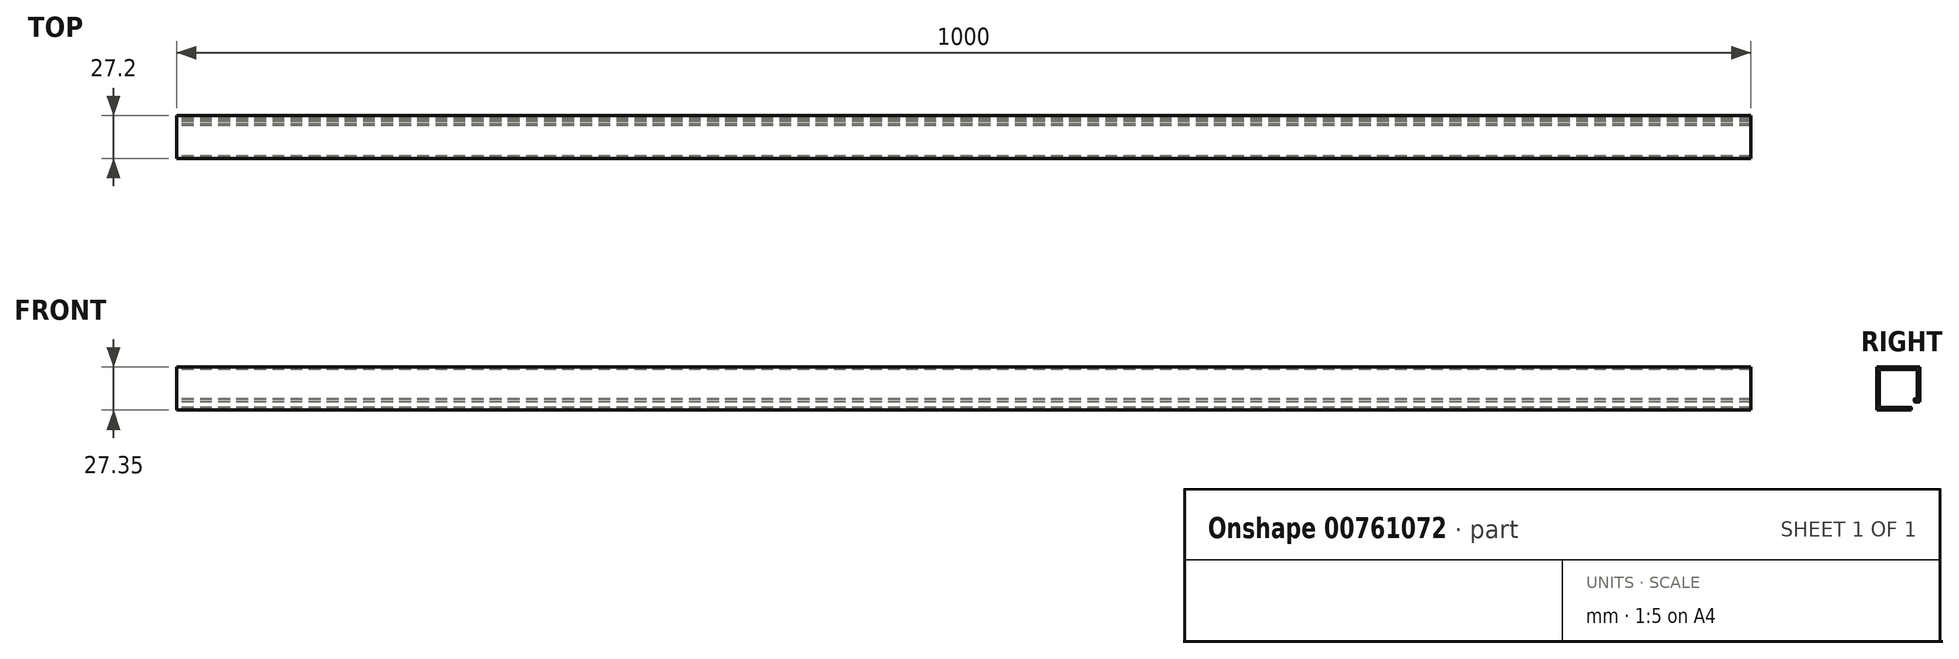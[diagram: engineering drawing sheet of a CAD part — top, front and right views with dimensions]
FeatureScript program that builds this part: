
annotation { "Feature Type Name" : "Feature", "Feature Type Description" : "" }
export const myFeature = defineFeature(function(context is Context, id is Id, definition is map)
    precondition{}
    {
        {
            var Q0;
            Q0=qCreatedBy(makeId("Right.planeOp"),FACE);
            var sketch = newSketch(context, id + "F0", { "sketchPlane" : qUnion([Q0])});
            skLineSegment(sketch, "E0.bottom", {"start": v(27.2, 27.35) * mm, "end": v(0, 27.35) * mm});
            skLineSegment(sketch, "E0.top", {"start": v(22, 0) * mm, "end": v(0, 0) * mm});
            skPoint(sketch, "E0.middle", {"position": v(0, 0) * mm});
            skLineSegment(sketch, "E1", {"start": v(22, 0) * mm, "end": v(22, 1.6) * mm});
            skLineSegment(sketch, "E2", {"start": v(1.6, 25.75) * mm, "end": v(25.6, 25.75) * mm});
            skLineSegment(sketch, "E3", {"start": v(27.2, 5.35) * mm, "end": v(27.2, 27.35) * mm});
            skPoint(sketch, "E4.orphan", {"position": v(13.3, 0) * mm});
            skLineSegment(sketch, "E5", {"start": v(22, 1.6) * mm, "end": v(22, 1.6) * mm});
            skLineSegment(sketch, "E6", {"start": v(21.75, 1.85) * mm, "end": v(21.37, 1.85) * mm});
            skPoint(sketch, "E7.start.orphan", {"position": v(12.8, 0) * mm});
            skLineSegment(sketch, "E8.trimOffspring", {"start": v(21, 1.6) * mm, "end": v(1.6, 1.6) * mm});
            skLineSegment(sketch, "E9.trimOffspring", {"start": v(25.6, 6.95) * mm, "end": v(25.6, 25.75) * mm});
            skLineSegment(sketch, "E10", {"start": v(27.2, 5.35) * mm, "end": v(24.1, 5.35) * mm});
            skLineSegment(sketch, "E11", {"start": v(23.6, 5.85) * mm, "end": v(23.6, 6.95) * mm});
            skLineSegment(sketch, "E12", {"start": v(23.85, 7.2) * mm, "end": v(24.33, 7.2) * mm});
            skLineSegment(sketch, "E13", {"start": v(24.7, 6.95) * mm, "end": v(25.6, 6.95) * mm});
            skPoint(sketch, "E14.visualSharp", {"position": v(23.6, 0) * mm});
            skArc(sketch, "E14.filletArc", {"start": v(23.6, 5.85) * mm, "mid": v(23.75, 5.5) * mm, "end": v(24.1, 5.35) * mm});
            skPoint(sketch, "E15.visualSharp", {"position": v(23.6, 7.2) * mm});
            skArc(sketch, "E15.filletArc", {"start": v(23.85, 7.2) * mm, "mid": v(23.67, 7.13) * mm, "end": v(23.6, 6.95) * mm});
            skPoint(sketch, "E16.visualSharp", {"position": v(9.15, 7.2) * mm});
            skArc(sketch, "E16.filletArc", {"start": v(24.7, 6.95) * mm, "mid": v(24.55, 7.13) * mm, "end": v(24.33, 7.2) * mm});
            skLineSegment(sketch, "E17", {"start": v(0, 0) * mm, "end": v(0, 27.35) * mm});
            skLineSegment(sketch, "E18", {"start": v(1.6, 25.75) * mm, "end": v(1.6, 13.67) * mm});
            skLineSegment(sketch, "E19", {"start": v(1.6, 13.67) * mm, "end": v(1.6, 1.6) * mm});
            skPoint(sketch, "E20.end.orphan", {"position": v(7.64, 6.95) * mm});
            skPoint(sketch, "E21.visualSharp", {"position": v(22, 1.85) * mm});
            skArc(sketch, "E21.filletArc", {"start": v(22, 1.6) * mm, "mid": v(21.93, 1.78) * mm, "end": v(21.75, 1.85) * mm});
            skPoint(sketch, "E22.visualSharp", {"position": v(7.03, 1.85) * mm});
            skArc(sketch, "E22.filletArc", {"start": v(21.37, 1.85) * mm, "mid": v(21.15, 1.78) * mm, "end": v(21, 1.6) * mm});
            skPoint(sketch, "E23.end.orphan", {"position": v(7.03, 1.6) * mm});
            skSolve(sketch);
        }
        {
            var Q0;
            Q0 = qSketchRegion(id + "F0", true);
            extrude(context, id + "F1", {"entities" : qUnion([Q0]), "depth" : 1000 * mm, "offsetDistance" : 25 * mm});
        }
    });
